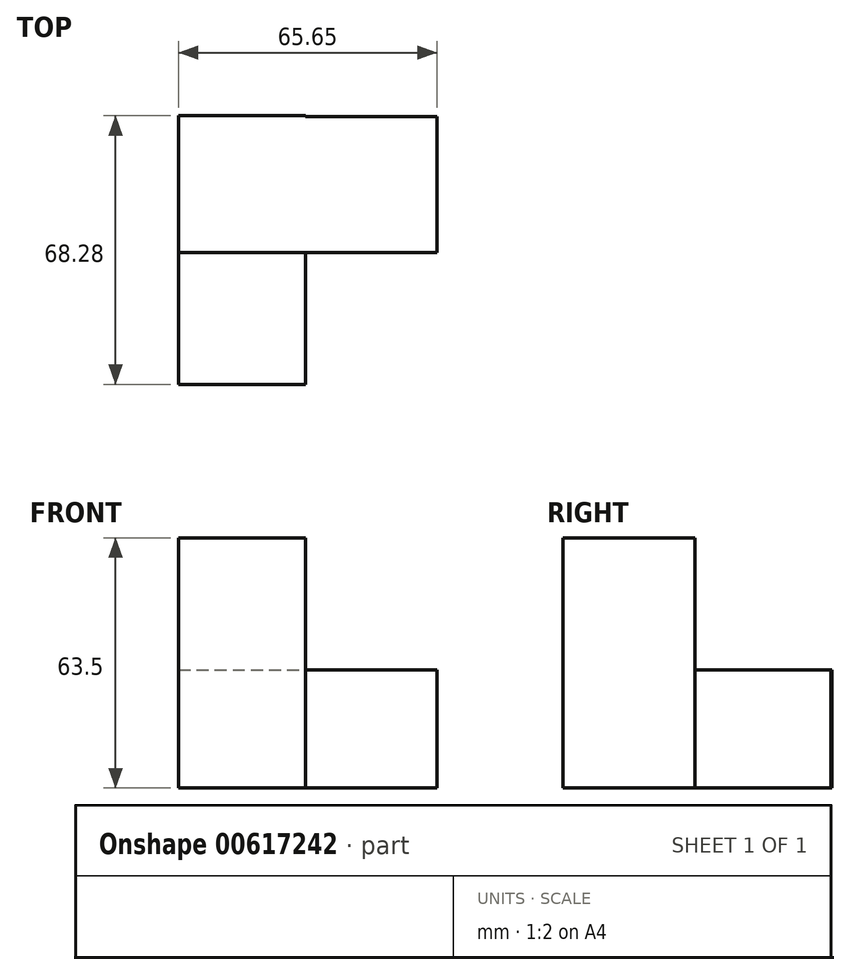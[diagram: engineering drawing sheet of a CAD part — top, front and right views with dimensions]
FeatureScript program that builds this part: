
annotation { "Feature Type Name" : "Feature", "Feature Type Description" : "" }
export const myFeature = defineFeature(function(context is Context, id is Id, definition is map)
    precondition{}
    {
        {
            var Q0;
            Q0=qCreatedBy(makeId("Top.planeOp"),FACE);
            var sketch = newSketch(context, id + "F0", { "sketchPlane" : qUnion([Q0])});
            skLineSegment(sketch, "E0.bottom", {"start": v(0, 0) * mm, "end": v(-32.3, 0) * mm});
            skLineSegment(sketch, "E0.top", {"start": v(0, 34.76) * mm, "end": v(-32.3, 34.76) * mm});
            skLineSegment(sketch, "E0.left", {"start": v(0, 0) * mm, "end": v(0, 34.76) * mm});
            skLineSegment(sketch, "E0.right", {"start": v(-32.3, 0) * mm, "end": v(-32.3, 34.76) * mm});
            skLineSegment(sketch, "E1.bottom", {"start": v(0, 0) * mm, "end": v(33.35, 0) * mm});
            skLineSegment(sketch, "E1.top", {"start": v(0, 34.57) * mm, "end": v(33.35, 34.57) * mm});
            skLineSegment(sketch, "E1.left", {"start": v(0, 0) * mm, "end": v(0, 34.57) * mm});
            skLineSegment(sketch, "E1.right", {"start": v(33.35, 0) * mm, "end": v(33.35, 34.57) * mm});
            skLineSegment(sketch, "E2.top", {"start": v(0, -33.52) * mm, "end": v(-32.3, -33.52) * mm});
            skLineSegment(sketch, "E2.left", {"start": v(0, 0) * mm, "end": v(0, -33.52) * mm});
            skLineSegment(sketch, "E2.right", {"start": v(-32.3, 0) * mm, "end": v(-32.3, -33.52) * mm});
            skSolve(sketch);
        }
        {
            var Q0;
            Q0 = qSketchRegion(id + "F0", true);
            extrude(context, id + "F1", {"entities" : qUnion([Q0]), "depth" : 29.97 * mm, "offsetDistance" : 25.4 * mm});
        }
        {
            var Q0;
            Q0=makeQuery(id+"F1.opExtrude","CAP_FACE",FACE,{"disambiguationData":[OSD([sQuery(id+"F0.wireOp",EDGE,"E0.top"),sQuery(id+"F0.wireOp",EDGE,"E0.left"),sQuery(id+"F0.wireOp",EDGE,"E0.right"),sQuery(id+"F0.wireOp",EDGE,"E1.bottom"),sQuery(id+"F0.wireOp",EDGE,"E1.top"),sQuery(id+"F0.wireOp",EDGE,"E1.right"),sQuery(id+"F0.wireOp",EDGE,"E0.bottom"),sQuery(id+"F0.wireOp",EDGE,"E2.top"),sQuery(id+"F0.wireOp",EDGE,"E2.left"),sQuery(id+"F0.wireOp",EDGE,"E2.right")])],"isStart":false});
            var sketch = newSketch(context, id + "F2", { "sketchPlane" : qUnion([Q0])});
            skLineSegment(sketch, "E3.bottom", {"start": v(-32.3, -33.52) * mm, "end": v(0, -33.52) * mm});
            skLineSegment(sketch, "E3.top", {"start": v(-32.3, 0) * mm, "end": v(0, 0) * mm});
            skLineSegment(sketch, "E3.left", {"start": v(-32.3, -33.52) * mm, "end": v(-32.3, 0) * mm});
            skLineSegment(sketch, "E3.right", {"start": v(0, -33.52) * mm, "end": v(0, 0) * mm});
            skSolve(sketch);
        }
        {
            var Q0;
            Q0=makeQuery(id+"F2.imprint","IMPRINT",FACE,{"disambiguationData":[TD([[makeQuery(id+"F2.imprint","IMPRINT",EDGE,{"derivedFrom":sQuery(id+"F2.wireOp",EDGE,"E3.bottom")}),-1.0]])]});
            extrude(context, id + "F3", {"entities" : qUnion([Q0]), "operationType" : NewBodyOperationType.ADD, "depth" : 33.53 * mm, "offsetDistance" : 25.4 * mm});
        }
    });
